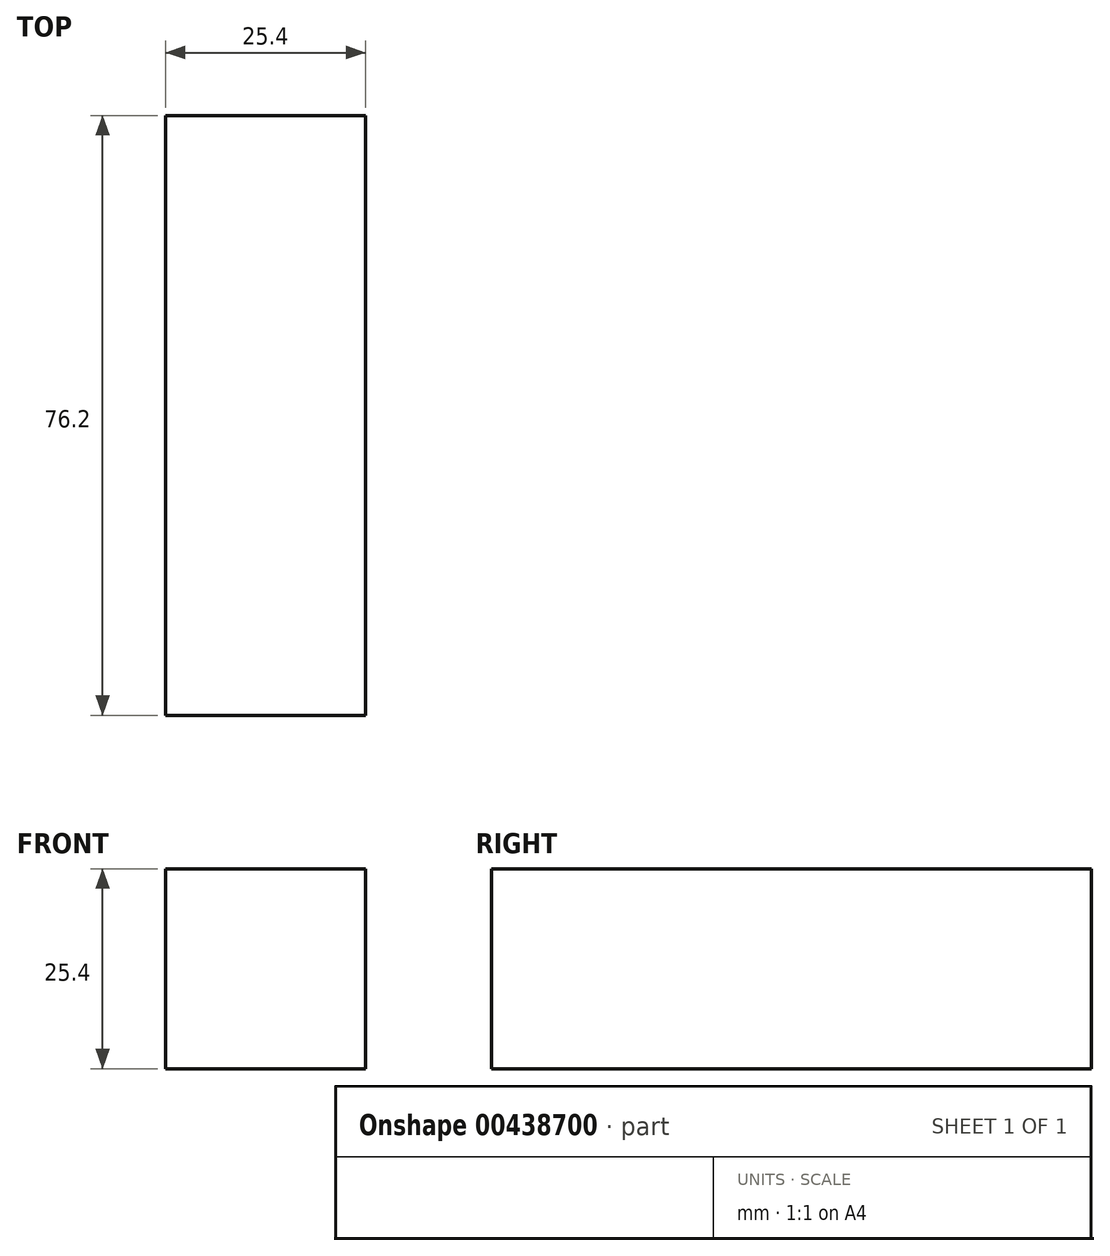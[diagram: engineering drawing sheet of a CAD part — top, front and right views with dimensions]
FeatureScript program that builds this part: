
annotation { "Feature Type Name" : "Feature", "Feature Type Description" : "" }
export const myFeature = defineFeature(function(context is Context, id is Id, definition is map)
    precondition{}
    {
        {
            var Q0;
            Q0=qCreatedBy(makeId("Front.planeOp"),FACE);
            var sketch = newSketch(context, id + "F0", { "sketchPlane" : qUnion([Q0])});
            skLineSegment(sketch, "E0", {"start": v(-25.4, 0) * mm, "end": v(0, 0) * mm});
            skLineSegment(sketch, "E1", {"start": v(0, 0) * mm, "end": v(0, 25.4) * mm});
            skLineSegment(sketch, "E2", {"start": v(0, 25.4) * mm, "end": v(-25.4, 25.4) * mm});
            skLineSegment(sketch, "E3", {"start": v(-25.4, 25.4) * mm, "end": v(-25.4, 0) * mm});
            skSolve(sketch);
        }
        {
            var Q0;
            Q0=makeQuery(id+"F0.imprint","IMPRINT",FACE,{"disambiguationData":[TD([[makeQuery(id+"F0.imprint","IMPRINT",EDGE,{"derivedFrom":sQuery(id+"F0.wireOp",EDGE,"E0")}),1.0]])]});
            extrude(context, id + "F1", {"entities" : qUnion([Q0]), "depth" : 76.2 * mm});
        }
    });
